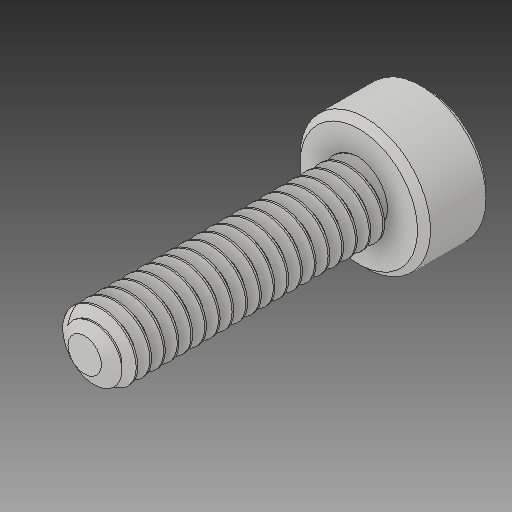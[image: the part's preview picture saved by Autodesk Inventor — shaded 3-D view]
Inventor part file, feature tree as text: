
AUTODESK INVENTOR PART (.ipt)
format: ipt  version: 2018 (Build 220112000, 112)  size: 788,992 bytes
history: native  units: in
note: dims shown in document units (in); Inventor stores cm internally (conversion verified against a paired STEP export)
features: chamfer x1
ambient origin geometry x8: Origin, YZ Plane, XZ Plane, XY Plane, X Axis, Y Axis, Z Axis, Center Point
bodies: Solid1 (feature_tree)
feature tree (1):
  chamfer  "Chamfer1"  [1 undecoded]
note: 1 required parameter value undecoded (feature->parameter linkage not recoverable at this tier; creation-order binding heuristic only, values carry confidence <= 0.55)
